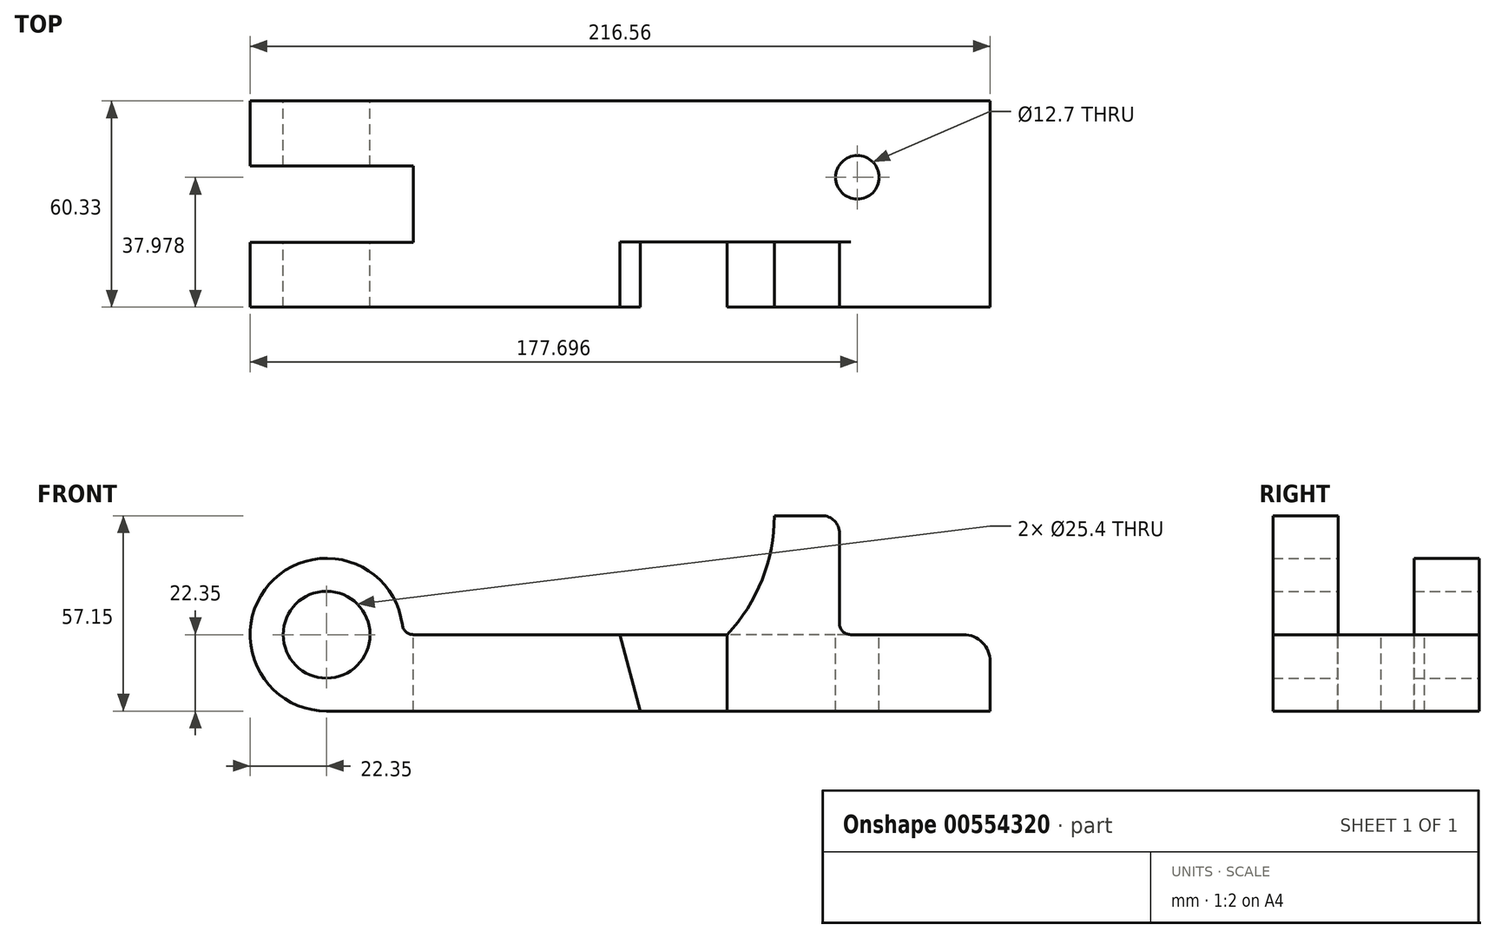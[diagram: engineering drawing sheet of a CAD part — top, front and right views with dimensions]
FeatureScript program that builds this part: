
annotation { "Feature Type Name" : "Feature", "Feature Type Description" : "" }
export const myFeature = defineFeature(function(context is Context, id is Id, definition is map)
    precondition{}
    {
        {
            var Q0;
            Q0=qCreatedBy(makeId("Front.planeOp"),FACE);
            var sketch = newSketch(context, id + "F0", { "sketchPlane" : qUnion([Q0])});
            skCircle(sketch, "E0", {"center": v(0, 0) * mm, "radius": 12.7 * mm});
            skArc(sketch, "E1", {"start": v(22.17, 2.88) * mm, "mid": v(-16.8, 14.75) * mm, "end": v(0, -22.35) * mm});
            skLineSegment(sketch, "E2", {"start": v(0, -22.35) * mm, "end": v(194.2, -22.35) * mm});
            skLineSegment(sketch, "E3", {"start": v(25.44, 0) * mm, "end": v(117.25, 0) * mm});
            skLineSegment(sketch, "E4", {"start": v(91.85, -22.35) * mm, "end": v(85.85, 0) * mm});
            skLineSegment(sketch, "E5", {"start": v(194.2, -22.35) * mm, "end": v(194.2, -7.87) * mm});
            skLineSegment(sketch, "E6", {"start": v(0, 34.8) * mm, "end": v(145, 34.8) * mm});
            skLineSegment(sketch, "E7", {"start": v(0, 34.8) * mm, "end": v(131.04, 34.8) * mm});
            skArc(sketch, "E8", {"start": v(117.25, 0) * mm, "mid": v(127.46, 16.08) * mm, "end": v(131.04, 34.8) * mm});
            skLineSegment(sketch, "E9", {"start": v(153.4, 0) * mm, "end": v(186.33, 0) * mm});
            skLineSegment(sketch, "E10", {"start": v(150.09, 29.72) * mm, "end": v(150.09, 3.3) * mm});
            skLineSegment(sketch, "E11", {"start": v(117.25, 0) * mm, "end": v(117.25, -22.35) * mm});
            skPoint(sketch, "E12.visualSharp", {"position": v(150.09, 0) * mm});
            skArc(sketch, "E12.filletArc", {"start": v(150.09, 3.3) * mm, "mid": v(151.06, 0.97) * mm, "end": v(153.4, 0) * mm});
            skPoint(sketch, "E13.visualSharp", {"position": v(150.09, 34.8) * mm});
            skArc(sketch, "E13.filletArc", {"start": v(150.09, 29.72) * mm, "mid": v(148.6, 33.31) * mm, "end": v(145, 34.8) * mm});
            skPoint(sketch, "E14.visualSharp", {"position": v(194.2, 0) * mm});
            skArc(sketch, "E14.filletArc", {"start": v(194.2, -7.87) * mm, "mid": v(191.9, -2.3) * mm, "end": v(186.33, 0) * mm});
            skPoint(sketch, "E15.visualSharp", {"position": v(22.35, 0) * mm});
            skArc(sketch, "E15.filletArc", {"start": v(22.17, 2.88) * mm, "mid": v(23.26, 0.82) * mm, "end": v(25.44, 0) * mm});
            skLineSegment(sketch, "E16", {"start": v(0, 0) * mm, "end": v(-22.35, 0) * mm});
            skSolve(sketch);
        }
        {
            var Q0;
            {var subQ0=sQuery(id+"F0.wireOp",EDGE,"E5");Q0=makeQuery(id+"F0.imprint","IMPRINT",FACE,{"disambiguationData":[TD([[makeQuery(id+"F0.imprint","IMPRINT",EDGE,{"derivedFrom":subQ0}),1.0]])]});}
            var Q1;
            {var subQ0=sQuery(id+"F0.wireOp",EDGE,"E4");Q1=makeQuery(id+"F0.imprint","IMPRINT",FACE,{"disambiguationData":[TD([[makeQuery(id+"F0.imprint","IMPRINT",EDGE,{"derivedFrom":subQ0}),-1.0]])]});}
            var Q2;
            Q2=makeQuery(id+"F0.imprint","IMPRINT",FACE,{"disambiguationData":[TD([[makeQuery(id+"F0.imprint","IMPRINT",EDGE,{"derivedFrom":sQuery(id+"F0.wireOp",EDGE,"E0")}),-1.0]])]});
            extrude(context, id + "F1", {"entities" : qUnion([Q0, Q1, Q2]), "depth" : 60.32 * mm, "offsetDistance" : 25 * mm});
        }
        {
            var Q0;
            Q0=makeQuery(id+"F1.opExtrude","SWEPT_FACE",FACE,{"disambiguationData":[OSD([sQuery(id+"F0.wireOp",EDGE,"E3")])]});
            var sketch = newSketch(context, id + "F2", { "sketchPlane" : qUnion([Q0])});
            skLineSegment(sketch, "E17.0", {"start": v(22.35, -60.33) * mm, "end": v(117.25, -60.33) * mm});
            skLineSegment(sketch, "E18", {"start": v(-23.99, -19) * mm, "end": v(25.44, -19) * mm});
            skLineSegment(sketch, "E19", {"start": v(-23.27, -41.33) * mm, "end": v(25.44, -41.33) * mm});
            skLineSegment(sketch, "E20", {"start": v(25.44, -19) * mm, "end": v(25.44, -41.33) * mm});
            skLineSegment(sketch, "E21", {"start": v(-23.99, -19) * mm, "end": v(-23.99, -41.33) * mm});
            skLineSegment(sketch, "E22", {"start": v(-23.99, -41.33) * mm, "end": v(-23.27, -41.33) * mm});
            skSolve(sketch);
        }
        {
            var Q0;
            Q0=qSketchRegion(id+"F2",true);
            extrude(context, id + "F3", {"entities" : qUnion([Q0]), "operationType" : NewBodyOperationType.REMOVE, "endBound" : BoundingType.SYMMETRIC, "oppositeDirection" : true, "depth" : 127.5 * mm, "offsetDistance" : 25 * mm});
        }
        {
            var Q0;
            Q0=makeQuery(id+"F1.opExtrude","SWEPT_FACE",FACE,{"disambiguationData":[OSD([sQuery(id+"F0.wireOp",EDGE,"E6")])]});
            var sketch = newSketch(context, id + "F4", { "sketchPlane" : qUnion([Q0])});
            skLineSegment(sketch, "E23", {"start": v(91.7, -60.33) * mm, "end": v(153.4, -60.33) * mm});
            skLineSegment(sketch, "E24", {"start": v(153.4, -60.33) * mm, "end": v(153.4, -41.28) * mm});
            skLineSegment(sketch, "E25", {"start": v(153.4, -41.27) * mm, "end": v(91.7, -41.27) * mm});
            skLineSegment(sketch, "E26", {"start": v(91.7, -41.28) * mm, "end": v(91.7, -60.33) * mm});
            skLineSegment(sketch, "E27.0", {"start": v(153.4, -60.33) * mm, "end": v(153.4, 0) * mm});
            skLineSegment(sketch, "E28", {"start": v(91.7, -41.27) * mm, "end": v(91.7, 0) * mm});
            skLineSegment(sketch, "E29", {"start": v(91.7, 0) * mm, "end": v(153.4, 0) * mm});
            skSolve(sketch);
        }
        {
            var Q0;
            {var subQ0=sQuery(id+"F4.wireOp",EDGE,"E28");Q0=makeQuery(id+"F4.imprint","IMPRINT",FACE,{"disambiguationData":[TD([[makeQuery(id+"F4.imprint","IMPRINT",EDGE,{"derivedFrom":subQ0}),-1.0]])]});}
            var Q1;
            {var subQ0=sQuery(id+"F4.wireOp",EDGE,"E25");var subQ1=sQuery(id+"F0.wireOp",EDGE,"E6");var subQ2=makeQuery(id+"F1.opExtrude","SWEPT_EDGE",EDGE,{"disambiguationData":[OSD([subQ1,sQuery(id+"F0.wireOp",EDGE,"E13.filletArc")])]});var subQ3=makeQuery(id+"F4.imprint","INTERSECT",VERTEX,{"derivedFrom":[subQ2,subQ0]});Q1=makeQuery(id+"F4.imprint","IMPRINT",FACE,{"disambiguationData":[TD([[makeQuery(id+"F4.imprint","IMPRINT",EDGE,{"disambiguationData":[TD([[subQ3,-1.0]])],"derivedFrom":subQ0}),-1.0]])]});}
            var Q2;
            {var subQ0=sQuery(id+"F4.wireOp",EDGE,"E27.0");var subQ1=sQuery(id+"F4.wireOp",EDGE,"E25");var subQ2=makeQuery(id+"F4.imprint","INTERSECT",VERTEX,{"derivedFrom":[subQ1,subQ0]});Q2=makeQuery(id+"F4.imprint","IMPRINT",FACE,{"disambiguationData":[TD([[makeQuery(id+"F4.imprint","IMPRINT",EDGE,{"disambiguationData":[TD([[subQ2,-1.0]])],"derivedFrom":subQ0}),1.0]])]});}
            extrude(context, id + "F5", {"entities" : qUnion([Q0, Q1, Q2]), "operationType" : NewBodyOperationType.REMOVE, "oppositeDirection" : true, "depth" : 34.8 * mm, "offsetDistance" : 25 * mm});
        }
        {
            var Q0;
            Q0=makeQuery(id+"F5.boolean.opBoolean","MERGE",FACE,{"derivedFrom":[makeQuery(id+"F1.opExtrude","SWEPT_FACE",FACE,{"disambiguationData":[OSD([sQuery(id+"F0.wireOp",EDGE,"E3")])]}),makeQuery(id+"F1.opExtrude","SWEPT_FACE",FACE,{"disambiguationData":[OSD([sQuery(id+"F0.wireOp",EDGE,"E9")])]}),makeQuery(id+"F5.opExtrude","CAP_FACE",FACE,{"disambiguationData":[OSD([sQuery(id+"F4.wireOp",EDGE,"E25"),sQuery(id+"F4.wireOp",EDGE,"E27.0"),sQuery(id+"F4.wireOp",EDGE,"E28"),sQuery(id+"F4.wireOp",EDGE,"E29")])],"isStart":false})]});
            var sketch = newSketch(context, id + "F6", { "sketchPlane" : qUnion([Q0])});
            skLineSegment(sketch, "E30.0", {"start": v(25.44, 0) * mm, "end": v(186.33, 0) * mm});
            skPoint(sketch, "E31.0", {"position": v(191.9, 0) * mm});
            skLineSegment(sketch, "E32.0", {"start": v(194.2, 0) * mm, "end": v(186.33, 0) * mm});
            skLineSegment(sketch, "E33", {"start": v(194.2, 0) * mm, "end": v(155.35, 0) * mm});
            skLineSegment(sketch, "E34", {"start": v(194.2, 0) * mm, "end": v(194.2, -22.35) * mm});
            skLineSegment(sketch, "E35", {"start": v(155.35, 0) * mm, "end": v(155.35, -22.35) * mm});
            skCircle(sketch, "E36", {"center": v(155.35, -22.35) * mm, "radius": 6.35 * mm});
            skSolve(sketch);
        }
        {
            var Q0;
            Q0=qSketchRegion(id+"F6",true);
            extrude(context, id + "F7", {"entities" : qUnion([Q0]), "operationType" : NewBodyOperationType.REMOVE, "endBound" : BoundingType.THROUGH_ALL, "oppositeDirection" : true, "depth" : 25.4 * mm});
        }
        {
            var Q0;
            Q0=makeQuery(id+"F1.opExtrude","CAP_FACE",FACE,{"disambiguationData":[OSD([sQuery(id+"F0.wireOp",EDGE,"E0"),sQuery(id+"F0.wireOp",EDGE,"E1"),sQuery(id+"F0.wireOp",EDGE,"E2"),sQuery(id+"F0.wireOp",EDGE,"E3"),sQuery(id+"F0.wireOp",EDGE,"E5"),sQuery(id+"F0.wireOp",EDGE,"E6"),sQuery(id+"F0.wireOp",EDGE,"E8"),sQuery(id+"F0.wireOp",EDGE,"E9"),sQuery(id+"F0.wireOp",EDGE,"E10"),sQuery(id+"F0.wireOp",EDGE,"E12.filletArc"),sQuery(id+"F0.wireOp",EDGE,"E13.filletArc"),sQuery(id+"F0.wireOp",EDGE,"E14.filletArc")])],"isStart":false});
            var sketch = newSketch(context, id + "F8", { "sketchPlane" : qUnion([Q0])});
            skLineSegment(sketch, "E37.0.0", {"start": v(117.25, -22.35) * mm, "end": v(117.25, 0) * mm});
            skLineSegment(sketch, "E37.0.1", {"start": v(117.25, 0) * mm, "end": v(85.85, 0) * mm});
            skLineSegment(sketch, "E37.0.2", {"start": v(85.85, 0) * mm, "end": v(91.85, -22.35) * mm});
            skLineSegment(sketch, "E37.0.3", {"start": v(91.85, -22.35) * mm, "end": v(117.25, -22.35) * mm});
            skSolve(sketch);
        }
        {
            var Q0;
            Q0=qSketchRegion(id+"F8",true);
            extrude(context, id + "F9", {"entities" : qUnion([Q0]), "operationType" : NewBodyOperationType.REMOVE, "oppositeDirection" : true, "depth" : 19.05 * mm});
        }
    });
